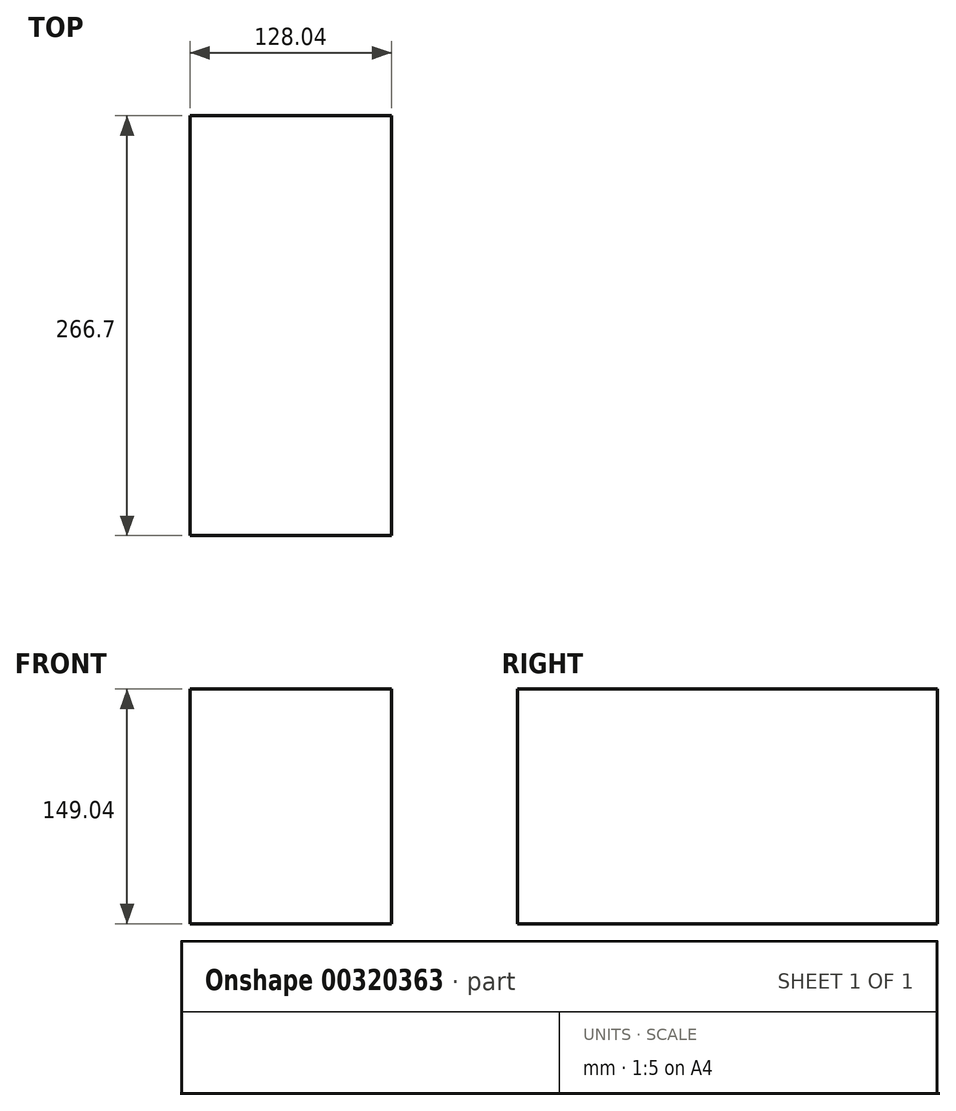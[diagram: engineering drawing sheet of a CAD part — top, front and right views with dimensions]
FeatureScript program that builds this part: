
annotation { "Feature Type Name" : "Feature", "Feature Type Description" : "" }
export const myFeature = defineFeature(function(context is Context, id is Id, definition is map)
    precondition{}
    {
        {
            var Q0;
            Q0=qCreatedBy(makeId("Front.planeOp"),FACE);
            var sketch = newSketch(context, id + "F0", { "sketchPlane" : qUnion([Q0])});
            skLineSegment(sketch, "E0.bottom", {"start": v(-62.88, 61.64) * mm, "end": v(65.16, 61.64) * mm});
            skLineSegment(sketch, "E0.top", {"start": v(-62.88, -62) * mm, "end": v(65.16, -62) * mm});
            skLineSegment(sketch, "E0.left", {"start": v(-62.88, 61.64) * mm, "end": v(-62.88, -62) * mm});
            skLineSegment(sketch, "E0.right", {"start": v(65.16, 61.64) * mm, "end": v(65.16, -62) * mm});
            skSolve(sketch);
        }
        {
            var Q0;
            Q0=makeQuery(id+"F0.imprint","IMPRINT",FACE,{"disambiguationData":[TD([[makeQuery(id+"F0.imprint","IMPRINT",EDGE,{"derivedFrom":sQuery(id+"F0.wireOp",EDGE,"E0.bottom")}),-1.0]])]});
            extrude(context, id + "F1", {"entities" : qUnion([Q0]), "oppositeDirection" : true, "depth" : 266.7 * mm});
        }
        {
            var Q0;
            Q0=makeQuery(id+"F1.opExtrude","SWEPT_FACE",FACE,{"disambiguationData":[OSD([sQuery(id+"F0.wireOp",EDGE,"E0.top")])]});
            var sketch = newSketch(context, id + "F2", { "sketchPlane" : qUnion([Q0])});
            skSolve(sketch);
        }
        {
            var Q0;
            {var subQ0=sQuery(id+"F0.wireOp",EDGE,"E0.top");Q0=makeQuery(id+"F2.imprint","IMPRINT",FACE,{"disambiguationData":[TD([[makeQuery(id+"F2.imprint","IMPRINT",EDGE,{"derivedFrom":makeQuery(id+"F1.opExtrude","CAP_EDGE",EDGE,{"disambiguationData":[OSD([subQ0])],"isStart":true})}),-1.0]])]});}
            extrude(context, id + "F3", {"entities" : qUnion([Q0]), "operationType" : NewBodyOperationType.ADD, "depth" : 25.4 * mm});
        }
    });
